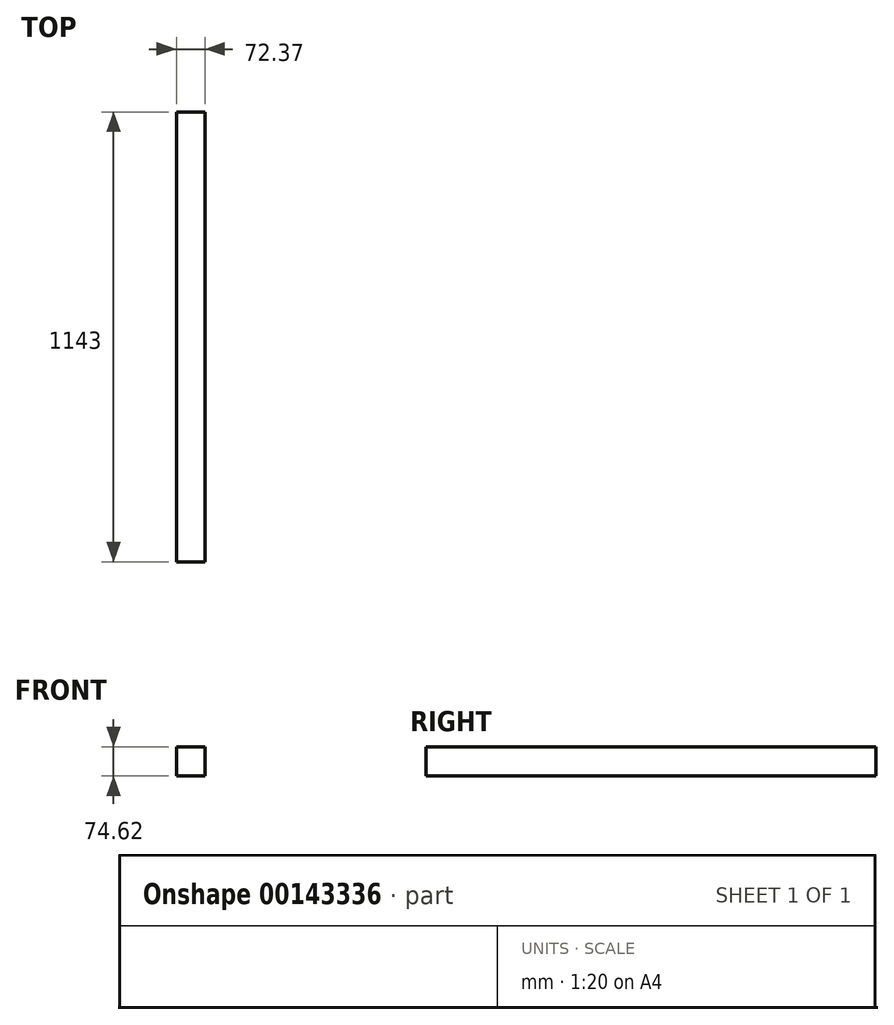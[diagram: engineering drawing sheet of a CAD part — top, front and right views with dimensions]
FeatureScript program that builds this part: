
annotation { "Feature Type Name" : "Feature", "Feature Type Description" : "" }
export const myFeature = defineFeature(function(context is Context, id is Id, definition is map)
    precondition{}
    {
        {
            var Q0;
            Q0=qCreatedBy(makeId("Front.planeOp"),FACE);
            var sketch = newSketch(context, id + "F0", { "sketchPlane" : qUnion([Q0])});
            skLineSegment(sketch, "E0.bottom", {"start": v(-49.6, 46.62) * mm, "end": v(22.77, 46.62) * mm});
            skLineSegment(sketch, "E0.top", {"start": v(-49.6, -28) * mm, "end": v(22.77, -28) * mm});
            skLineSegment(sketch, "E0.left", {"start": v(-49.6, 46.62) * mm, "end": v(-49.6, -28) * mm});
            skLineSegment(sketch, "E0.right", {"start": v(22.77, 46.62) * mm, "end": v(22.77, -28) * mm});
            skSolve(sketch);
        }
        {
            var Q0;
            Q0=makeQuery(id+"F0.imprint","IMPRINT",FACE,{"disambiguationData":[TD([[makeQuery(id+"F0.imprint","IMPRINT",EDGE,{"derivedFrom":sQuery(id+"F0.wireOp",EDGE,"E0.bottom")}),-1.0]])]});
            extrude(context, id + "F1", {"entities" : qUnion([Q0]), "depth" : 1143 * mm});
        }
    });
